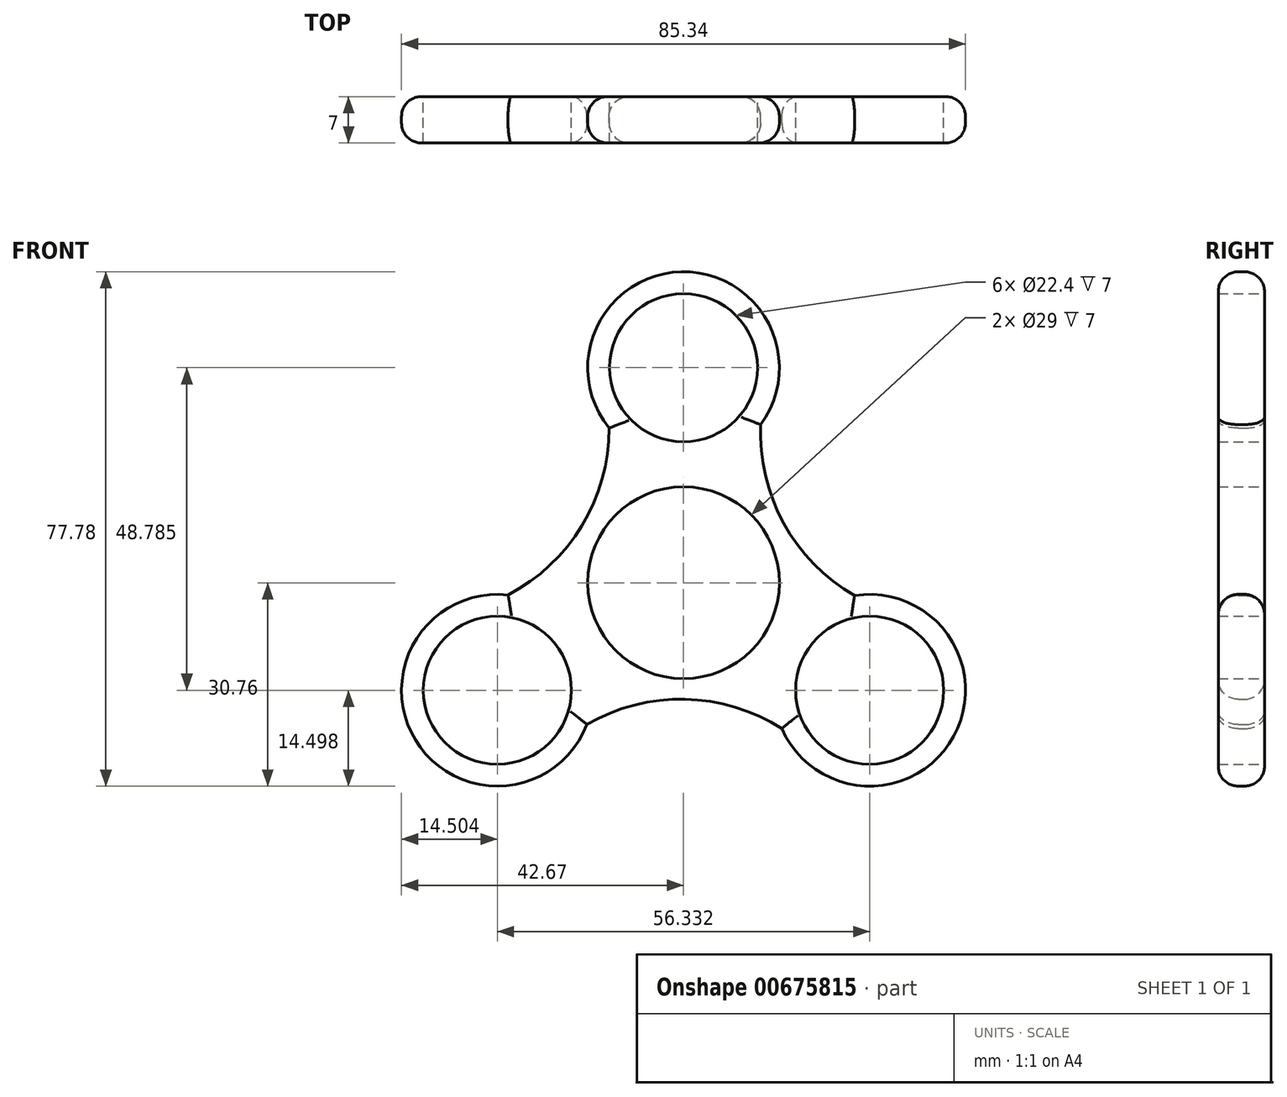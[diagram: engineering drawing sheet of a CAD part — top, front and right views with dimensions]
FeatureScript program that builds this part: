
annotation { "Feature Type Name" : "Feature", "Feature Type Description" : "" }
export const myFeature = defineFeature(function(context is Context, id is Id, definition is map)
    precondition{}
    {
        {
            var Q0;
            Q0=qCreatedBy(makeId("Front.planeOp"),FACE);
            var sketch = newSketch(context, id + "F0", { "sketchPlane" : qUnion([Q0])});
            skCircle(sketch, "E0", {"center": v(0, 0) * mm, "radius": 11.2 * mm});
            skCircle(sketch, "E1", {"center": v(0, 0) * mm, "radius": 14.5 * mm});
            skCircle(sketch, "E2", {"center": v(0, 32.52) * mm, "radius": 11.2 * mm});
            skCircle(sketch, "E3", {"center": v(0, 32.52) * mm, "radius": 14.5 * mm});
            skCircle(sketch, "E4.1.0", {"center": v(-28.17, -16.26) * mm, "radius": 11.2 * mm});
            skCircle(sketch, "E4.1.1", {"center": v(-28.17, -16.26) * mm, "radius": 14.5 * mm});
            skCircle(sketch, "E4.2.0", {"center": v(28.17, -16.26) * mm, "radius": 11.2 * mm});
            skCircle(sketch, "E4.2.1", {"center": v(28.17, -16.26) * mm, "radius": 14.5 * mm});
            skLineSegment(sketch, "E5", {"start": v(-28.17, -16.26) * mm, "end": v(0, 0) * mm, "construction": true});
            skLineSegment(sketch, "E6", {"start": v(0, 0) * mm, "end": v(37.7, 21.77) * mm, "construction": true});
            skLineSegment(sketch, "E7", {"start": v(0, 32.52) * mm, "end": v(28.17, -16.26) * mm, "construction": true});
            skArc(sketch, "E8", {"start": v(11.67, 23.92) * mm, "mid": v(15.16, 9) * mm, "end": v(25.9, -1.94) * mm});
            skArc(sketch, "E9.1.0", {"start": v(-26.55, -1.85) * mm, "mid": v(-15.37, 8.63) * mm, "end": v(-11.27, 23.4) * mm});
            skArc(sketch, "E9.2.0", {"start": v(14.88, -22.07) * mm, "mid": v(0.21, -17.62) * mm, "end": v(-14.63, -21.45) * mm});
            skSolve(sketch);
        }
        {
            var Q0;
            Q0 = qSketchRegion(id + "F0", true);
            extrude(context, id + "F1", {"entities" : qUnion([Q0]), "depth" : 7 * mm, "offsetDistance" : 25 * mm});
        }
        {
            var Q0;
            Q0=makeQuery(id+"F1.opExtrude","CAP_EDGE",EDGE,{"disambiguationData":[OSD([sQuery(id+"F0.wireOp",EDGE,"E9.2.0")])],"isStart":false});
            var Q1;
            Q1=makeQuery(id+"F1.opExtrude","CAP_EDGE",EDGE,{"disambiguationData":[OSD([sQuery(id+"F0.wireOp",EDGE,"E8")])],"isStart":false});
            var Q2;
            Q2=makeQuery(id+"F1.opExtrude","CAP_EDGE",EDGE,{"disambiguationData":[OSD([sQuery(id+"F0.wireOp",EDGE,"E9.1.0")])],"isStart":false});
            var Q3;
            Q3=makeQuery(id+"F1.opExtrude","CAP_EDGE",EDGE,{"disambiguationData":[OSD([sQuery(id+"F0.wireOp",EDGE,"E4.2.1")])],"isStart":false});
            var Q4;
            Q4=makeQuery(id+"F1.opExtrude","CAP_EDGE",EDGE,{"disambiguationData":[OSD([sQuery(id+"F0.wireOp",EDGE,"E4.1.1")])],"isStart":false});
            var Q5;
            Q5=makeQuery(id+"F1.opExtrude","CAP_EDGE",EDGE,{"disambiguationData":[OSD([sQuery(id+"F0.wireOp",EDGE,"E3")])],"isStart":false});
            var Q6;
            Q6=makeQuery(id+"F1.opExtrude","CAP_EDGE",EDGE,{"disambiguationData":[OSD([sQuery(id+"F0.wireOp",EDGE,"E9.1.0")])],"isStart":true});
            var Q7;
            Q7=makeQuery(id+"F1.opExtrude","CAP_EDGE",EDGE,{"disambiguationData":[OSD([sQuery(id+"F0.wireOp",EDGE,"E8")])],"isStart":true});
            var Q8;
            Q8=makeQuery(id+"F1.opExtrude","CAP_EDGE",EDGE,{"disambiguationData":[OSD([sQuery(id+"F0.wireOp",EDGE,"E9.2.0")])],"isStart":true});
            var Q9;
            Q9=makeQuery(id+"F1.opExtrude","CAP_EDGE",EDGE,{"disambiguationData":[OSD([sQuery(id+"F0.wireOp",EDGE,"E3")])],"isStart":true});
            var Q10;
            Q10=makeQuery(id+"F1.opExtrude","CAP_EDGE",EDGE,{"disambiguationData":[OSD([sQuery(id+"F0.wireOp",EDGE,"E4.1.1")])],"isStart":true});
            var Q11;
            Q11=makeQuery(id+"F1.opExtrude","CAP_EDGE",EDGE,{"disambiguationData":[OSD([sQuery(id+"F0.wireOp",EDGE,"E4.2.1")])],"isStart":true});
            fillet(context, id + "F2", {"entities" : qUnion([Q0, Q1, Q2, Q3, Q4, Q5, Q6, Q7, Q8, Q9, Q10, Q11]), "radius" : 3 * mm, "tangentPropagation" : true, "allowEdgeOverflow" : false});
        }
    });
